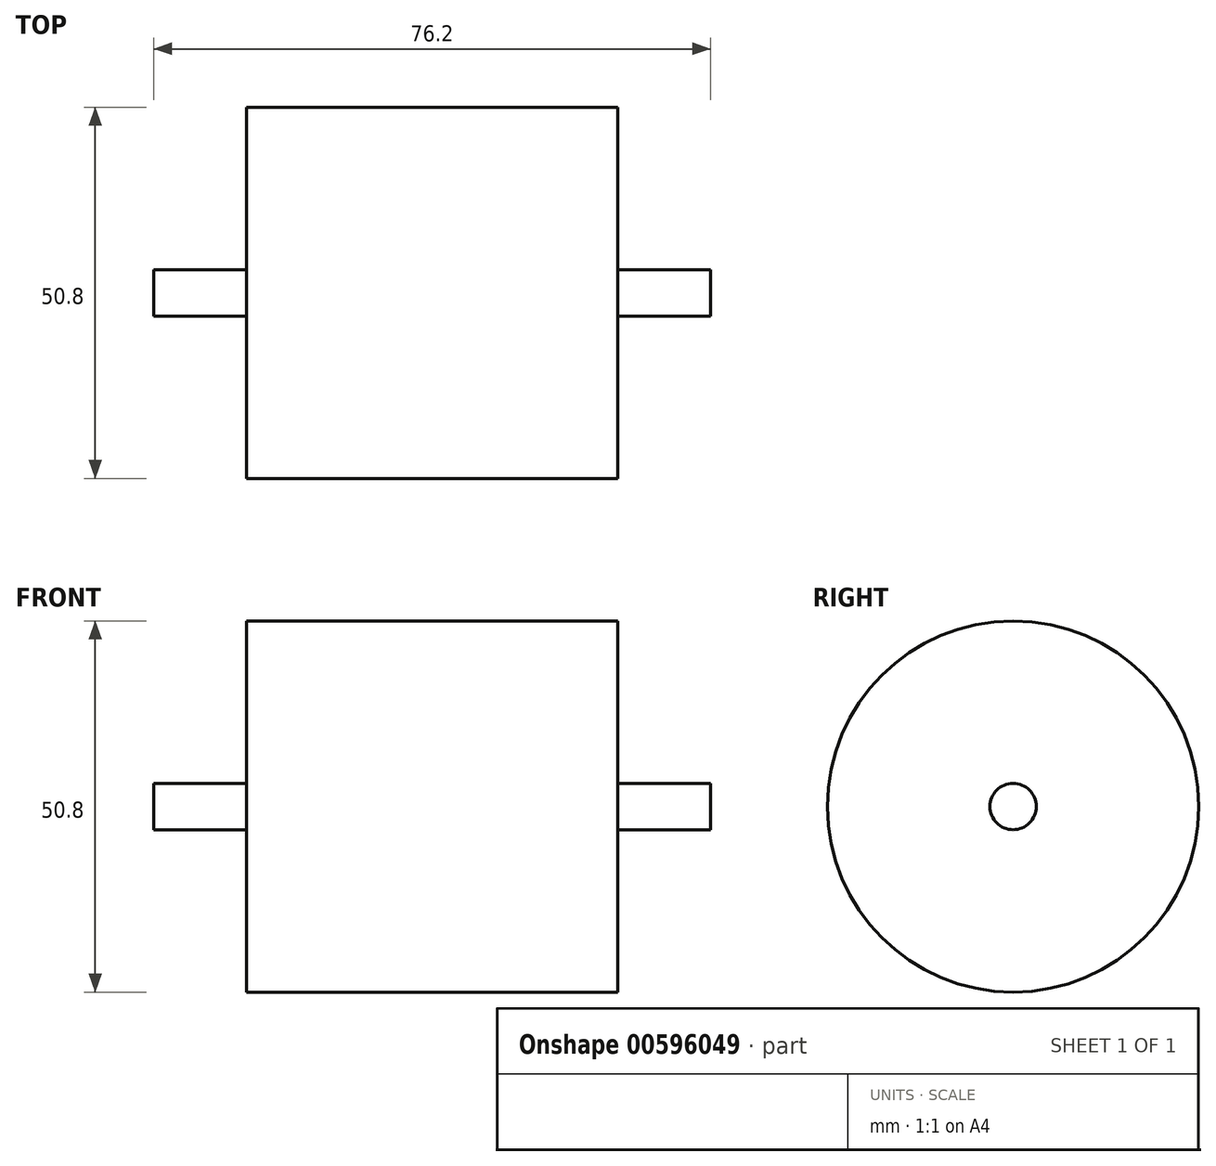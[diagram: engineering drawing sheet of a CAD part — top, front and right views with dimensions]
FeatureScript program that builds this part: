
annotation { "Feature Type Name" : "Feature", "Feature Type Description" : "" }
export const myFeature = defineFeature(function(context is Context, id is Id, definition is map)
    precondition{}
    {
        {
            var Q0;
            Q0=qCreatedBy(makeId("Right.planeOp"),FACE);
            var sketch = newSketch(context, id + "F0", { "sketchPlane" : qUnion([Q0])});
            skCircle(sketch, "E0", {"center": v(0, 0) * mm, "radius": 25.4 * mm});
            skSolve(sketch);
        }
        {
            var Q0;
            Q0 = qSketchRegion(id + "F0", true);
            extrude(context, id + "F1", {"entities" : qUnion([Q0]), "depth" : 25.4 * mm, "offsetDistance" : 25.4 * mm});
        }
        {
            var Q0;
            Q0=makeQuery(id+"F1.opExtrude","CAP_FACE",FACE,{"disambiguationData":[OSD([sQuery(id+"F0.wireOp",EDGE,"E0")])],"isStart":false});
            var sketch = newSketch(context, id + "F2", { "sketchPlane" : qUnion([Q0])});
            skCircle(sketch, "E1", {"center": v(0, 0) * mm, "radius": 3.18 * mm});
            skSolve(sketch);
        }
        {
            var Q0;
            Q0 = qSketchRegion(id + "F2", true);
            extrude(context, id + "F3", {"entities" : qUnion([Q0]), "operationType" : NewBodyOperationType.ADD, "depth" : 12.7 * mm, "offsetDistance" : 25.4 * mm});
        }
        {
            var Q0;
            Q0=makeQuery(id+"F1.opExtrude","SWEPT_BODY",BODY,{"disambiguationData":[OSD([sQuery(id+"F0.wireOp",EDGE,"E0")])]});
            var Q1;
            Q1=qCreatedBy(makeId("Right.planeOp"),FACE);
            mirror(context, id + "F4", {"operationType" : NewBodyOperationType.ADD, "entities" : qUnion([Q0]), "mirrorPlane" : qUnion([Q1])});
        }
    });
